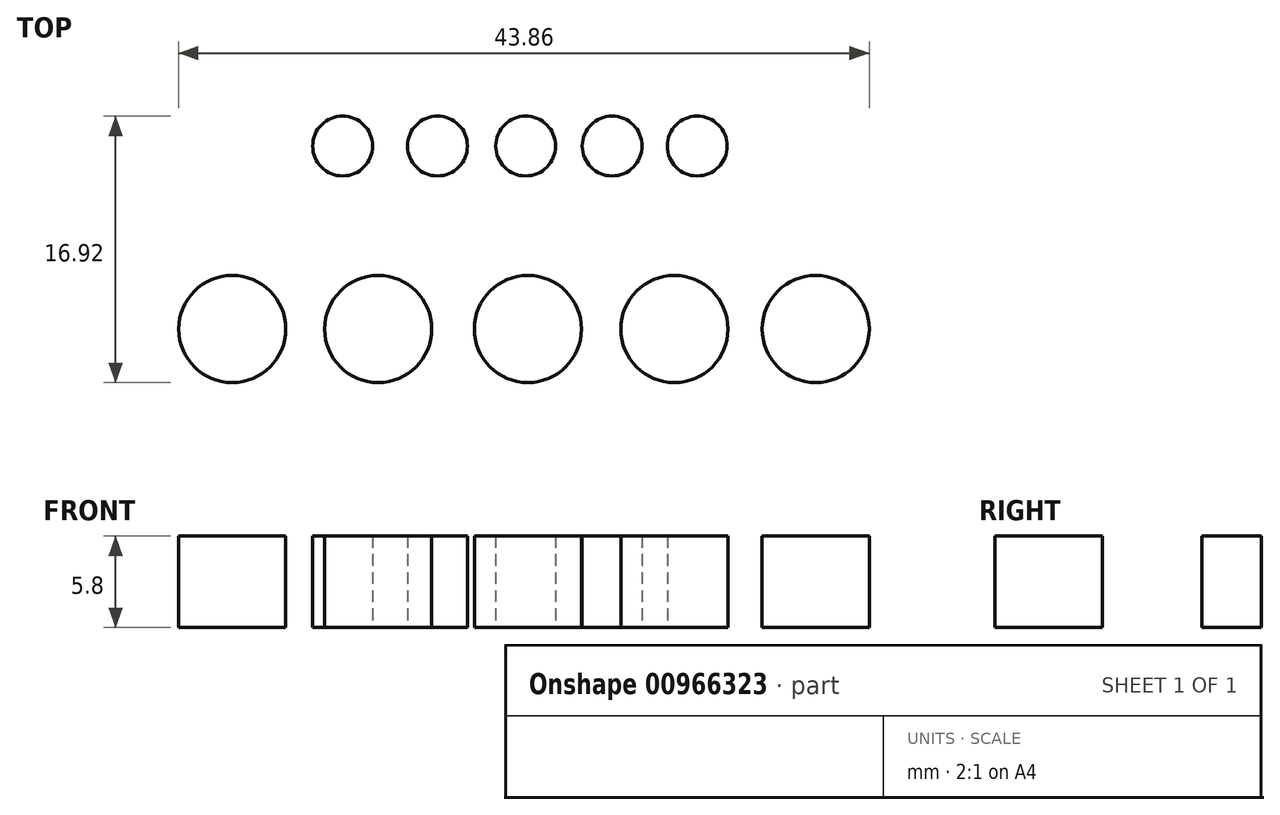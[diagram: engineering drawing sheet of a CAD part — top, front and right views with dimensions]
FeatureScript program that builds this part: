
annotation { "Feature Type Name" : "Feature", "Feature Type Description" : "" }
export const myFeature = defineFeature(function(context is Context, id is Id, definition is map)
    precondition{}
    {
        {
            var Q0;
            Q0=qCreatedBy(makeId("Top.planeOp"),FACE);
            var sketch = newSketch(context, id + "F0", { "sketchPlane" : qUnion([Q0])});
            skCircle(sketch, "E0", {"center": v(10.9, 17.77) * mm, "radius": 1.9 * mm});
            skCircle(sketch, "E1", {"center": v(18.42, 6.15) * mm, "radius": 3.4 * mm});
            skCircle(sketch, "E2", {"center": v(9.45, 6.15) * mm, "radius": 3.4 * mm});
            skCircle(sketch, "E3", {"center": v(0.14, 6.15) * mm, "radius": 3.4 * mm});
            skCircle(sketch, "E4", {"center": v(-9.37, 6.15) * mm, "radius": 3.4 * mm});
            skCircle(sketch, "E5", {"center": v(-18.64, 6.15) * mm, "radius": 3.4 * mm});
            skCircle(sketch, "E6", {"center": v(5.5, 17.77) * mm, "radius": 1.9 * mm});
            skCircle(sketch, "E7", {"center": v(0, 17.77) * mm, "radius": 1.9 * mm});
            skCircle(sketch, "E8", {"center": v(-5.6, 17.77) * mm, "radius": 1.9 * mm});
            skCircle(sketch, "E9", {"center": v(-11.62, 17.77) * mm, "radius": 1.9 * mm});
            skSolve(sketch);
        }
        {
            var Q0;
            Q0 = qSketchRegion(id + "F0", true);
            extrude(context, id + "F1", {"entities" : qUnion([Q0]), "depth" : 5.8 * mm, "offsetDistance" : 25 * mm});
        }
    });
